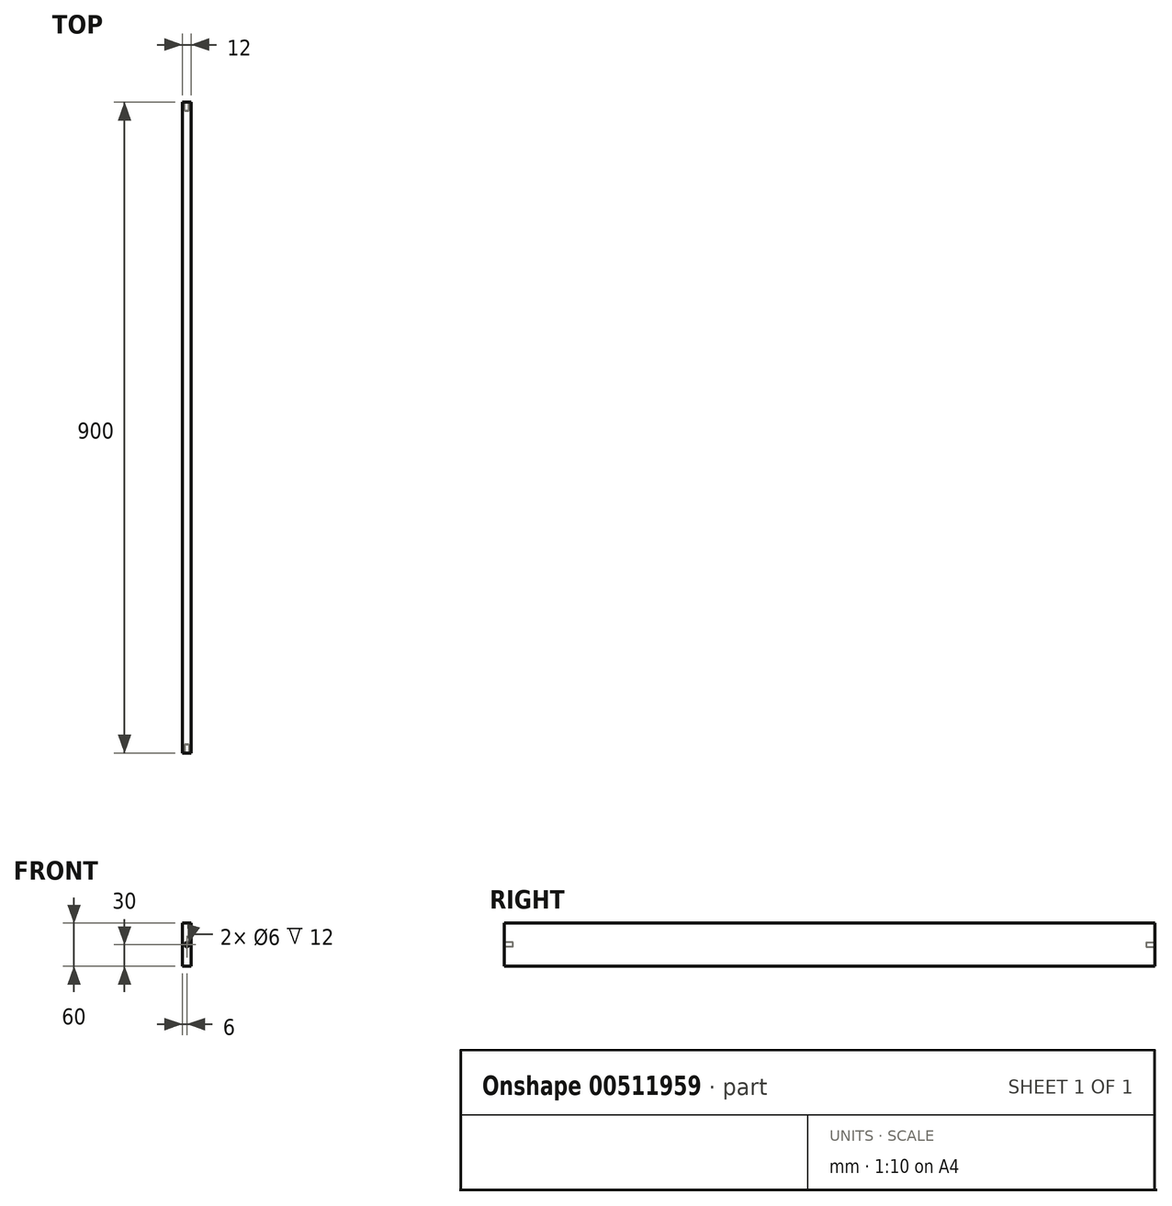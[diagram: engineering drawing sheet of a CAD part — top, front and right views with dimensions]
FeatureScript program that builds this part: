
annotation { "Feature Type Name" : "Feature", "Feature Type Description" : "" }
export const myFeature = defineFeature(function(context is Context, id is Id, definition is map)
    precondition{}
    {
        {
            var Q0;
            Q0=qCreatedBy(makeId("Front.planeOp"),FACE);
            var sketch = newSketch(context, id + "F0", { "sketchPlane" : qUnion([Q0])});
            skLineSegment(sketch, "E0.bottom", {"start": v(0, 0) * mm, "end": v(-12, 0) * mm});
            skLineSegment(sketch, "E0.top", {"start": v(0, 60) * mm, "end": v(-12, 60) * mm});
            skLineSegment(sketch, "E0.left", {"start": v(0, 0) * mm, "end": v(0, 60) * mm});
            skLineSegment(sketch, "E0.right", {"start": v(-12, 0) * mm, "end": v(-12, 60) * mm});
            skSolve(sketch);
        }
        {
            var Q0;
            Q0=makeQuery(id+"F0.imprint","IMPRINT",FACE,{"disambiguationData":[TD([[makeQuery(id+"F0.imprint","IMPRINT",EDGE,{"derivedFrom":sQuery(id+"F0.wireOp",EDGE,"E0.bottom")}),-1.0]])]});
            extrude(context, id + "F1", {"entities" : qUnion([Q0]), "depth" : 900 * mm, "offsetDistance" : 25 * mm, "symmetric" : true});
        }
        {
            var Q0;
            Q0=makeQuery(id+"F1.opExtrude","CAP_FACE",FACE,{"disambiguationData":[OSD([sQuery(id+"F0.wireOp",EDGE,"E0.bottom"),sQuery(id+"F0.wireOp",EDGE,"E0.top"),sQuery(id+"F0.wireOp",EDGE,"E0.left"),sQuery(id+"F0.wireOp",EDGE,"E0.right")])],"isStart":false});
            var sketch = newSketch(context, id + "F2", { "sketchPlane" : qUnion([Q0])});
            skCircle(sketch, "E1", {"center": v(-6, 30) * mm, "radius": 3 * mm});
            skSolve(sketch);
        }
        {
            var Q0;
            Q0=makeQuery(id+"F2.imprint","IMPRINT",FACE,{"disambiguationData":[TD([[makeQuery(id+"F2.imprint","IMPRINT",EDGE,{"derivedFrom":sQuery(id+"F2.wireOp",EDGE,"E1")}),1.0]])]});
            extrude(context, id + "F3", {"entities" : qUnion([Q0]), "operationType" : NewBodyOperationType.REMOVE, "oppositeDirection" : true, "depth" : 12 * mm, "offsetDistance" : 25 * mm});
        }
        {
            var Q0;
            Q0=makeQuery(id+"F1.opExtrude","CAP_FACE",FACE,{"disambiguationData":[OSD([sQuery(id+"F0.wireOp",EDGE,"E0.bottom"),sQuery(id+"F0.wireOp",EDGE,"E0.top"),sQuery(id+"F0.wireOp",EDGE,"E0.left"),sQuery(id+"F0.wireOp",EDGE,"E0.right")])],"isStart":true});
            var sketch = newSketch(context, id + "F4", { "sketchPlane" : qUnion([Q0])});
            skCircle(sketch, "E2.0.0", {"center": v(6, 30) * mm, "radius": 3 * mm});
            skSolve(sketch);
        }
        {
            var Q0;
            Q0=makeQuery(id+"F4.imprint","IMPRINT",FACE,{"disambiguationData":[TD([[makeQuery(id+"F4.imprint","IMPRINT",EDGE,{"derivedFrom":sQuery(id+"F4.wireOp",EDGE,"E2.0.0")}),1.0]])]});
            extrude(context, id + "F5", {"entities" : qUnion([Q0]), "operationType" : NewBodyOperationType.REMOVE, "oppositeDirection" : true, "depth" : 12 * mm, "offsetDistance" : 25 * mm});
        }
    });
